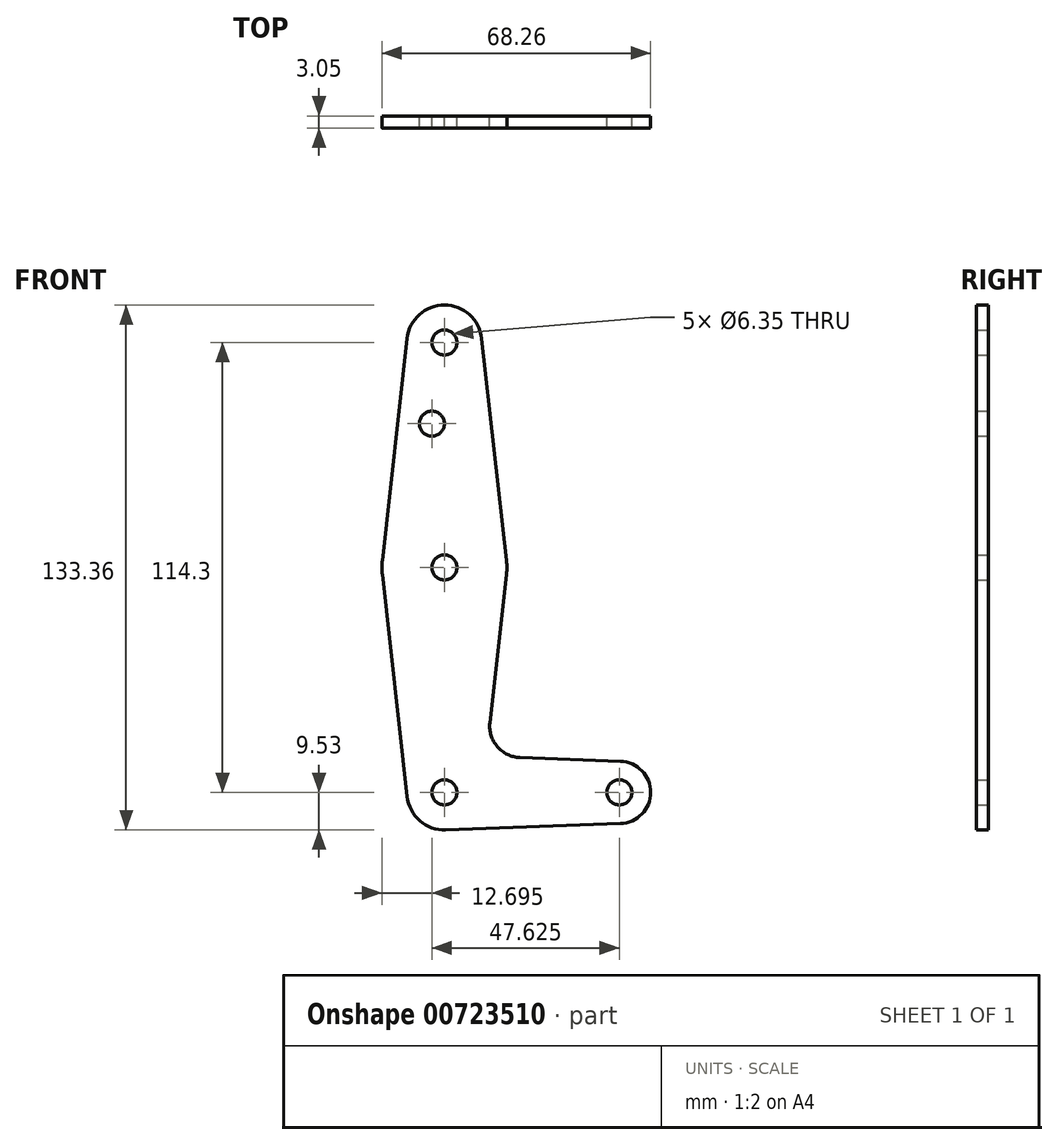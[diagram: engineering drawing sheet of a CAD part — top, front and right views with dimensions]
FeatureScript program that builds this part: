
annotation { "Feature Type Name" : "Feature", "Feature Type Description" : "" }
export const myFeature = defineFeature(function(context is Context, id is Id, definition is map)
    precondition{}
    {
        {
            var Q0;
            Q0=qCreatedBy(makeId("Front.planeOp"),FACE);
            var sketch = newSketch(context, id + "F0", { "sketchPlane" : qUnion([Q0])});
            skLineSegment(sketch, "E0", {"start": v(0, 114.3) * mm, "end": v(0, 0) * mm, "construction": true});
            skLineSegment(sketch, "E1", {"start": v(44.45, 0) * mm, "end": v(0, 0) * mm, "construction": true});
            skCircle(sketch, "E2", {"center": v(0, 114.3) * mm, "radius": 9.53 * mm});
            skCircle(sketch, "E3", {"center": v(0, 0) * mm, "radius": 9.53 * mm});
            skCircle(sketch, "E4", {"center": v(0, 57.15) * mm, "radius": 15.88 * mm});
            skCircle(sketch, "E5", {"center": v(44.45, 0) * mm, "radius": 7.94 * mm});
            skCircle(sketch, "E6", {"center": v(0, 114.3) * mm, "radius": 3.18 * mm});
            skCircle(sketch, "E7", {"center": v(0, 57.15) * mm, "radius": 3.18 * mm});
            skCircle(sketch, "E8", {"center": v(0, 0) * mm, "radius": 3.18 * mm});
            skCircle(sketch, "E9", {"center": v(44.45, 0) * mm, "radius": 3.18 * mm});
            skPoint(sketch, "E10.orphan", {"position": v(-9.53, 114.3) * mm});
            skLineSegment(sketch, "E11", {"start": v(9.47, 115.36) * mm, "end": v(15.78, 58.91) * mm});
            skLineSegment(sketch, "E12", {"start": v(-9.47, 115.36) * mm, "end": v(-15.78, 58.91) * mm});
            skCircle(sketch, "E13", {"center": v(-3.17, 93.68) * mm, "radius": 3.18 * mm});
            skLineSegment(sketch, "E14", {"start": v(-15.78, 55.39) * mm, "end": v(-9.47, -1.06) * mm});
            skLineSegment(sketch, "E15", {"start": v(15.78, 55.39) * mm, "end": v(11.56, 17.67) * mm});
            skLineSegment(sketch, "E16", {"start": v(19.18, 8.85) * mm, "end": v(44.73, 7.93) * mm});
            skLineSegment(sketch, "E17", {"start": v(0.34, -9.52) * mm, "end": v(44.73, -7.93) * mm});
            skArc(sketch, "E18.filletArc", {"start": v(11.56, 17.67) * mm, "mid": v(13.44, 11.6) * mm, "end": v(19.18, 8.85) * mm});
            skSolve(sketch);
        }
        {
            var Q0;
            Q0 = qSketchRegion(id + "F0", true);
            extrude(context, id + "F1", {"entities" : qUnion([Q0]), "depth" : 3.05 * mm, "offsetDistance" : 25.4 * mm});
        }
    });
